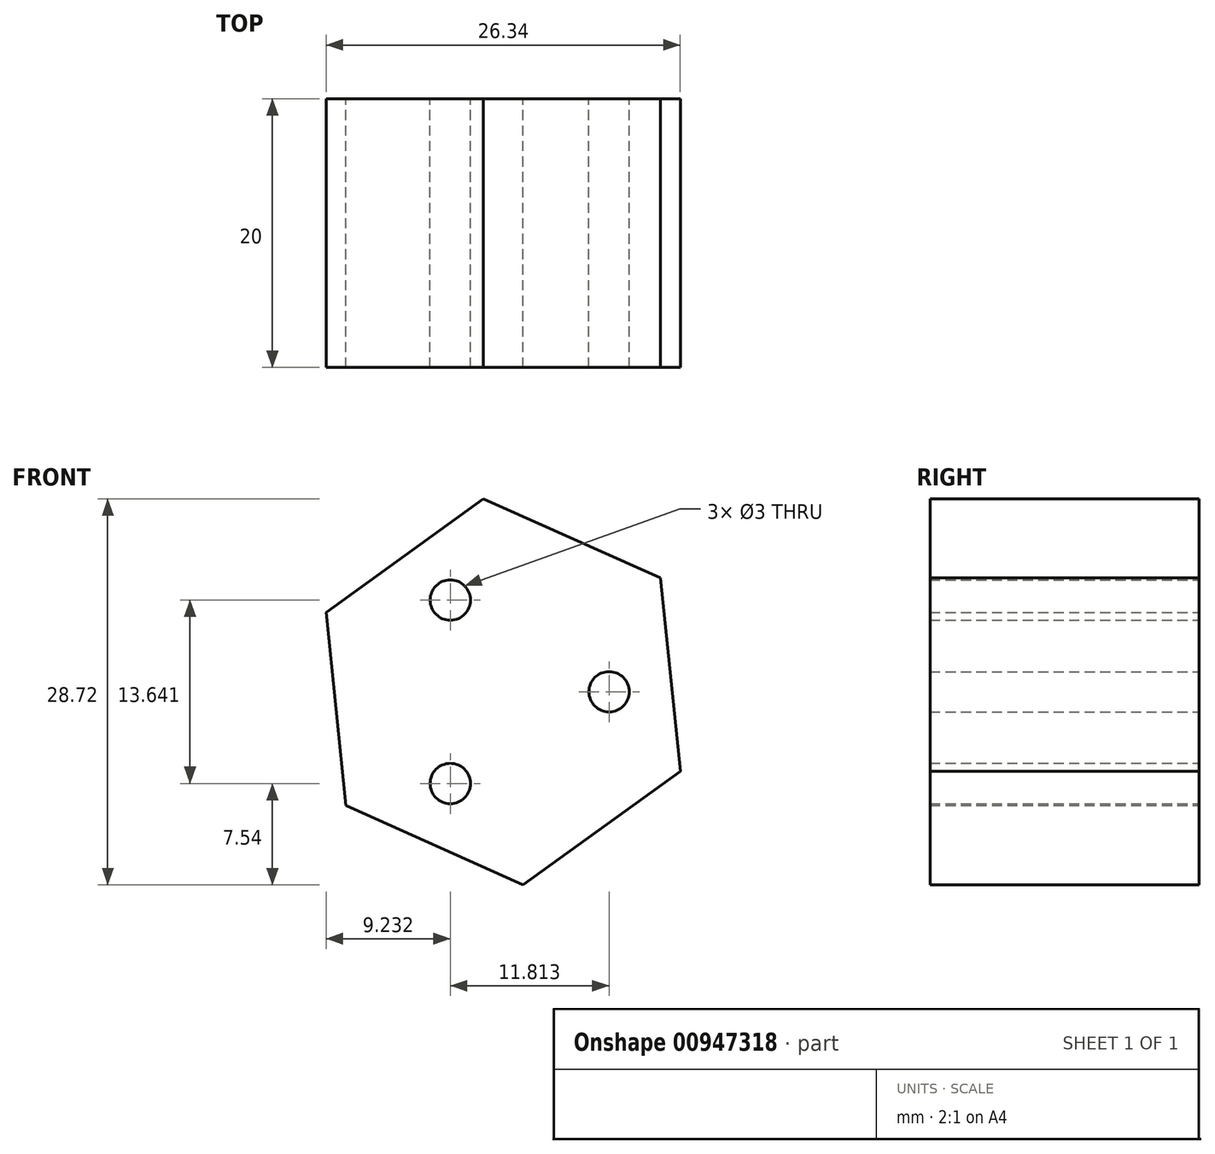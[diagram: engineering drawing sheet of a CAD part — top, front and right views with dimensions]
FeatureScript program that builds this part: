
annotation { "Feature Type Name" : "Feature", "Feature Type Description" : "" }
export const myFeature = defineFeature(function(context is Context, id is Id, definition is map)
    precondition{}
    {
        {
            var Q0;
            Q0=qCreatedBy(makeId("Front.planeOp"),FACE);
            var sketch = newSketch(context, id + "F0", { "sketchPlane" : qUnion([Q0])});
            skCircle(sketch, "E0.cCircle", {"center": v(0, 0) * mm, "radius": 14.43 * mm, "construction": true});
            skLineSegment(sketch, "E0.0", {"start": v(13.17, -5.9) * mm, "end": v(1.48, -14.36) * mm});
            skLineSegment(sketch, "E0.1", {"start": v(1.48, -14.36) * mm, "end": v(-11.7, -8.46) * mm});
            skLineSegment(sketch, "E0.2", {"start": v(-11.7, -8.46) * mm, "end": v(-13.17, 5.9) * mm});
            skLineSegment(sketch, "E0.3", {"start": v(-13.17, 5.9) * mm, "end": v(-1.48, 14.36) * mm});
            skLineSegment(sketch, "E0.4", {"start": v(-1.48, 14.36) * mm, "end": v(11.7, 8.46) * mm});
            skLineSegment(sketch, "E0.5", {"start": v(11.7, 8.46) * mm, "end": v(13.17, -5.9) * mm});
            skSolve(sketch);
        }
        {
            var Q0;
            Q0=makeQuery(id+"F0.imprint","IMPRINT",FACE,{"disambiguationData":[TD([[makeQuery(id+"F0.imprint","IMPRINT",EDGE,{"derivedFrom":sQuery(id+"F0.wireOp",EDGE,"E0.0")}),-1.0]])]});
            extrude(context, id + "F1", {"entities" : qUnion([Q0]), "depth" : 20 * mm, "offsetDistance" : 25 * mm});
        }
        {
            var Q0;
            Q0=makeQuery(id+"F1.opExtrude","CAP_FACE",FACE,{"disambiguationData":[OSD([sQuery(id+"F0.wireOp",EDGE,"E0.0"),sQuery(id+"F0.wireOp",EDGE,"E0.1"),sQuery(id+"F0.wireOp",EDGE,"E0.2"),sQuery(id+"F0.wireOp",EDGE,"E0.3"),sQuery(id+"F0.wireOp",EDGE,"E0.4"),sQuery(id+"F0.wireOp",EDGE,"E0.5")])],"isStart":true});
            var sketch = newSketch(context, id + "F2", { "sketchPlane" : qUnion([Q0])});
            skPoint(sketch, "E1", {"position": v(-7.88, 0) * mm});
            skPoint(sketch, "E2.1.0", {"position": v(3.94, -6.82) * mm});
            skPoint(sketch, "E2.2.0", {"position": v(3.94, 6.82) * mm});
            skPoint(sketch, "E2.center", {"position": v(0, 0) * mm});
            skSolve(sketch);
        }
        {
            var Q0;
            Q0=sQuery(id+"F2.wireOp",VERTEX,"E2.1.0");
            var Q1;
            Q1=sQuery(id+"F2.wireOp",VERTEX,"E2.2.0");
            var Q2;
            Q2=sQuery(id+"F2.wireOp",VERTEX,"E1");
            var Q3;
            Q3=makeQuery(id+"F1.opExtrude","SWEPT_BODY",BODY,{"disambiguationData":[OSD([sQuery(id+"F0.wireOp",EDGE,"E0.0"),sQuery(id+"F0.wireOp",EDGE,"E0.1"),sQuery(id+"F0.wireOp",EDGE,"E0.2"),sQuery(id+"F0.wireOp",EDGE,"E0.3"),sQuery(id+"F0.wireOp",EDGE,"E0.4"),sQuery(id+"F0.wireOp",EDGE,"E0.5")])]});
            hole(context, id + "F3", {"style" : HoleStyle.SIMPLE, "endStyle" : HoleEndStyle.THROUGH, "holeDiameter" : 3 * mm, "majorDiameter" : 5 * mm, "isTappedThrough" : true, "tappedDepth" : 12 * mm, "tapClearance" : 3, "locations" : qUnion([Q0, Q1, Q2]), "scope" : qUnion([Q3])});
        }
    });
